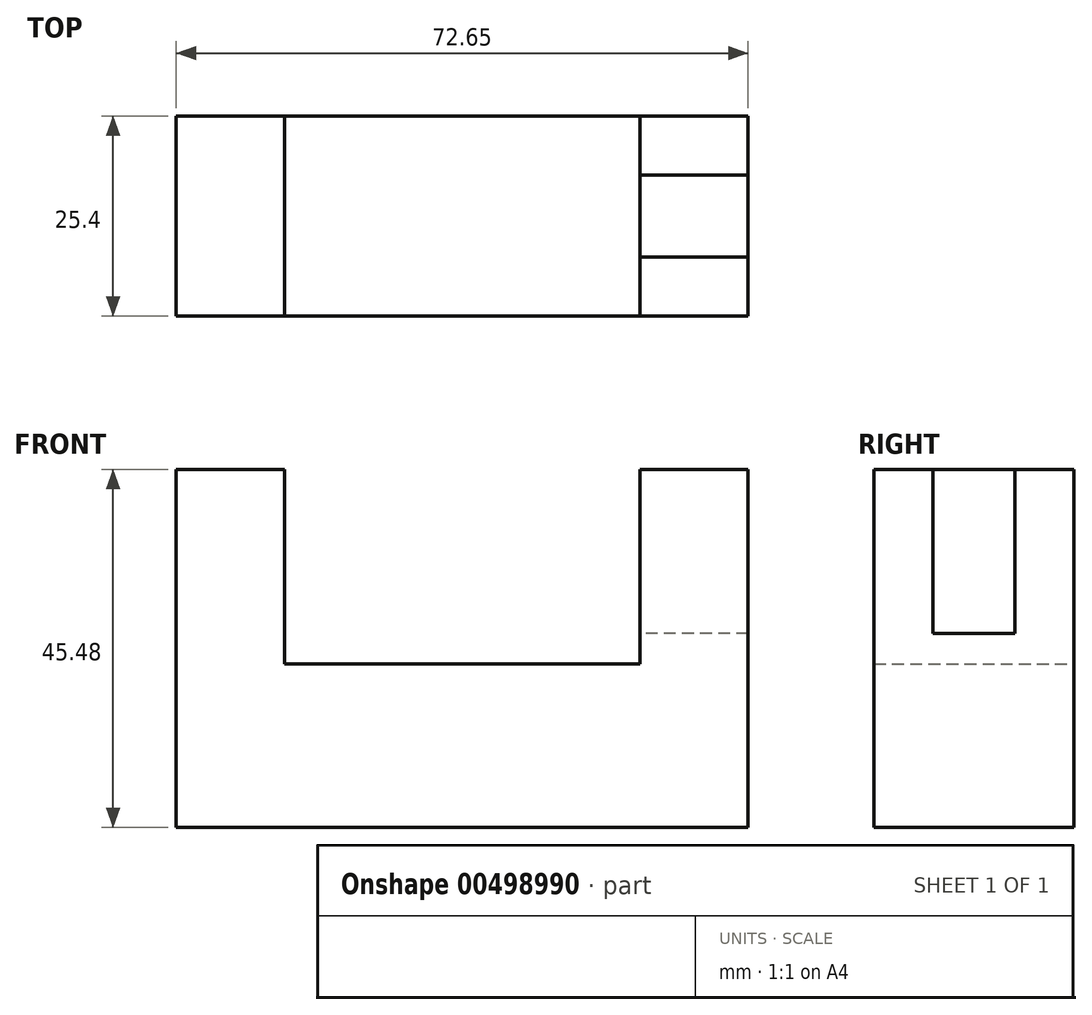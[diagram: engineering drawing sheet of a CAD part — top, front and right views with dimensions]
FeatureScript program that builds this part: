
annotation { "Feature Type Name" : "Feature", "Feature Type Description" : "" }
export const myFeature = defineFeature(function(context is Context, id is Id, definition is map)
    precondition{}
    {
        {
            var Q0;
            Q0=qCreatedBy(makeId("Front.planeOp"),FACE);
            var sketch = newSketch(context, id + "F0", { "sketchPlane" : qUnion([Q0])});
            skLineSegment(sketch, "E0.bottom", {"start": v(0, 0) * mm, "end": v(72.65, 0) * mm});
            skLineSegment(sketch, "E0.top", {"start": v(0, 45.48) * mm, "end": v(13.74, 45.48) * mm});
            skLineSegment(sketch, "E0.left", {"start": v(0, 0) * mm, "end": v(0, 45.48) * mm});
            skLineSegment(sketch, "E0.right", {"start": v(72.65, 0) * mm, "end": v(72.65, 45.48) * mm});
            skLineSegment(sketch, "E1.top", {"start": v(13.74, 20.76) * mm, "end": v(58.92, 20.76) * mm});
            skLineSegment(sketch, "E1.left", {"start": v(13.74, 45.48) * mm, "end": v(13.74, 20.76) * mm});
            skLineSegment(sketch, "E1.right", {"start": v(58.92, 45.48) * mm, "end": v(58.92, 20.76) * mm});
            skLineSegment(sketch, "E2.trimOffspring", {"start": v(58.92, 45.48) * mm, "end": v(72.65, 45.48) * mm});
            skSolve(sketch);
        }
        {
            var Q0;
            Q0=makeQuery(id+"F0.imprint","IMPRINT",FACE,{"disambiguationData":[TD([[makeQuery(id+"F0.imprint","IMPRINT",EDGE,{"derivedFrom":sQuery(id+"F0.wireOp",EDGE,"E0.bottom")}),1.0]])]});
            extrude(context, id + "F1", {"entities" : qUnion([Q0]), "depth" : 25.4 * mm, "offsetDistance" : 25.4 * mm});
        }
        {
            var Q0;
            Q0=makeQuery(id+"F1.opExtrude","SWEPT_FACE",FACE,{"disambiguationData":[OSD([sQuery(id+"F0.wireOp",EDGE,"E2.trimOffspring")])]});
            var sketch = newSketch(context, id + "F2", { "sketchPlane" : qUnion([Q0])});
            skLineSegment(sketch, "E3.bottom", {"start": v(72.65, -7.49) * mm, "end": v(58.92, -7.49) * mm});
            skLineSegment(sketch, "E3.top", {"start": v(72.65, -17.91) * mm, "end": v(58.92, -17.91) * mm});
            skLineSegment(sketch, "E3.left", {"start": v(72.65, -7.49) * mm, "end": v(72.65, -17.91) * mm});
            skLineSegment(sketch, "E3.right", {"start": v(58.92, -7.49) * mm, "end": v(58.92, -17.91) * mm});
            skPoint(sketch, "E3.middle", {"position": v(65.79, -12.7) * mm});
            skPoint(sketch, "E3.middle.positionSnap0", {"position": v(65.79, -25.4) * mm});
            skPoint(sketch, "E3.middle.positionSnap1", {"position": v(58.92, -12.7) * mm});
            skPoint(sketch, "E3.centerSnap0", {"position": v(65.79, -25.4) * mm});
            skPoint(sketch, "E3.centerSnap1", {"position": v(58.92, -12.7) * mm});
            skSolve(sketch);
        }
        {
            var Q0;
            Q0 = qSketchRegion(id + "F2", true);
            extrude(context, id + "F3", {"entities" : qUnion([Q0]), "operationType" : NewBodyOperationType.REMOVE, "oppositeDirection" : true, "depth" : 20.83 * mm, "offsetDistance" : 25.4 * mm});
        }
    });
